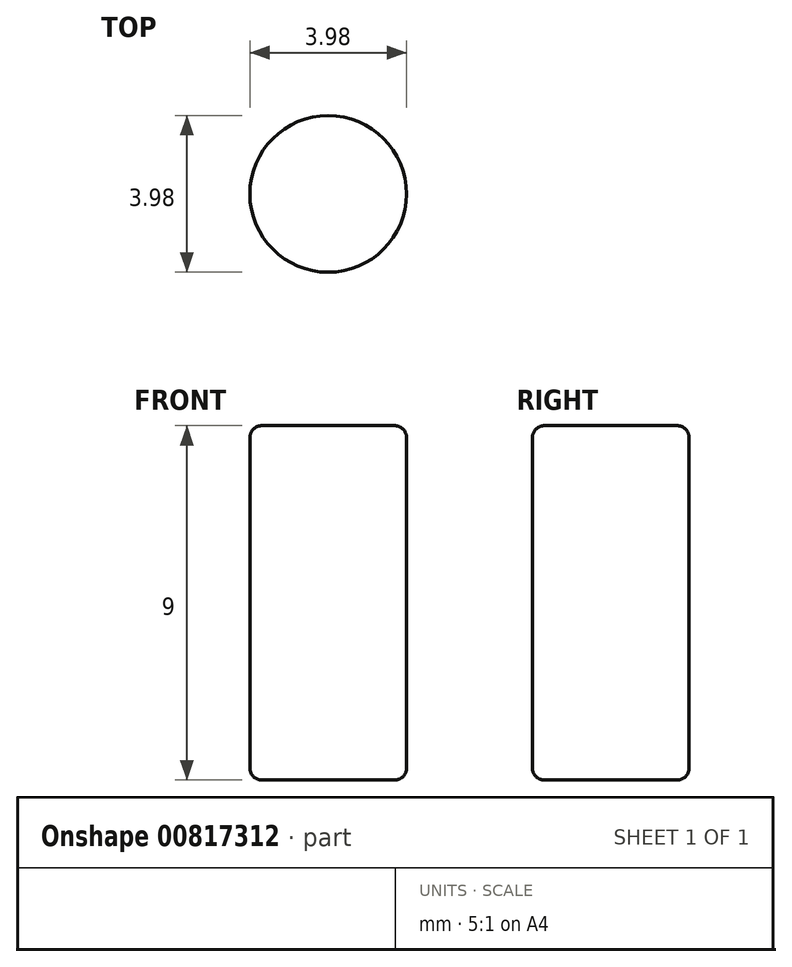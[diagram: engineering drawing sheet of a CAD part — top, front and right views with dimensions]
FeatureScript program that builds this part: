
annotation { "Feature Type Name" : "Feature", "Feature Type Description" : "" }
export const myFeature = defineFeature(function(context is Context, id is Id, definition is map)
    precondition{}
    {
        {
            var Q0;
            Q0=qCreatedBy(makeId("Top.planeOp"),FACE);
            var sketch = newSketch(context, id + "F0", { "sketchPlane" : qUnion([Q0])});
            skCircle(sketch, "E0", {"center": v(0, 0) * mm, "radius": 1.99 * mm});
            skSolve(sketch);
        }
        {
            var Q0;
            Q0=makeQuery(id+"F0.imprint","IMPRINT",FACE,{"disambiguationData":[TD([[makeQuery(id+"F0.imprint","IMPRINT",EDGE,{"derivedFrom":sQuery(id+"F0.wireOp",EDGE,"E0")}),1.0]])]});
            extrude(context, id + "F1", {"entities" : qUnion([Q0]), "depth" : 9 * mm, "offsetDistance" : 25 * mm});
        }
        {
            var Q0;
            Q0=makeQuery(id+"F1.opExtrude","CAP_FACE",FACE,{"disambiguationData":[OSD([sQuery(id+"F0.wireOp",EDGE,"E0")])],"isStart":false});
            var Q1;
            Q1=makeQuery(id+"F1.opExtrude","CAP_FACE",FACE,{"disambiguationData":[OSD([sQuery(id+"F0.wireOp",EDGE,"E0")])],"isStart":true});
            fillet(context, id + "F2", {"entities" : qUnion([Q0, Q1]), "radius" : .3 * mm, "tangentPropagation" : true, "allowEdgeOverflow" : false});
        }
    });
